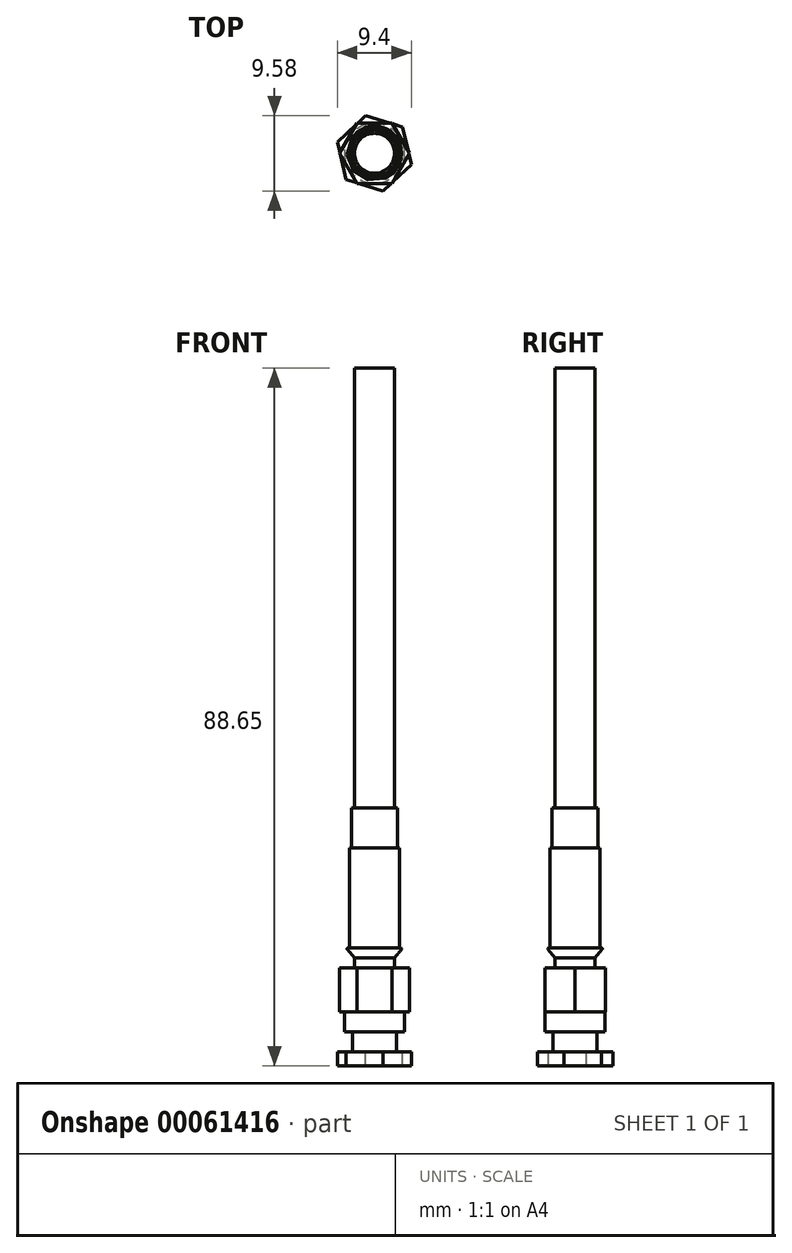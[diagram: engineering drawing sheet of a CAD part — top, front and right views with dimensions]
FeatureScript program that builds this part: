
annotation { "Feature Type Name" : "Feature", "Feature Type Description" : "" }
export const myFeature = defineFeature(function(context is Context, id is Id, definition is map)
    precondition{}
    {
        {
            var Q0;
            Q0=qCreatedBy(makeId("Top.planeOp"),FACE);
            var sketch = newSketch(context, id + "F0", { "sketchPlane" : qUnion([Q0])});
            skCircle(sketch, "E0", {"center": v(0, 0) * mm, "radius": 2.54 * mm});
            skSolve(sketch);
        }
        {
            var Q0;
            Q0 = qSketchRegion(id + "F0", true);
            extrude(context, id + "F1", {"entities" : qUnion([Q0]), "depth" : 76.2 * mm});
        }
        {
            var Q0;
            Q0=qCreatedBy(makeId("Top.planeOp"),FACE);
            var sketch = newSketch(context, id + "F2", { "sketchPlane" : qUnion([Q0])});
            skCircle(sketch, "E1.cCircle", {"center": v(0, 0) * mm, "radius": 3.85 * mm, "construction": true});
            skLineSegment(sketch, "E1.0", {"start": v(4.45, 0) * mm, "end": v(2.22, -3.85) * mm});
            skLineSegment(sketch, "E1.1", {"start": v(2.22, -3.85) * mm, "end": v(-2.22, -3.85) * mm});
            skLineSegment(sketch, "E1.2", {"start": v(-2.22, -3.85) * mm, "end": v(-4.45, 0) * mm});
            skLineSegment(sketch, "E1.3", {"start": v(-4.44, 0) * mm, "end": v(-2.22, 3.85) * mm});
            skLineSegment(sketch, "E1.4", {"start": v(-2.22, 3.85) * mm, "end": v(2.22, 3.85) * mm});
            skLineSegment(sketch, "E1.5", {"start": v(2.22, 3.85) * mm, "end": v(4.44, 0) * mm});
            skPoint(sketch, "E1.0.midPoint", {"position": v(3.33, -1.92) * mm});
            skSolve(sketch);
        }
        {
            var Q0;
            Q0 = qSketchRegion(id + "F2", true);
            extrude(context, id + "F3", {"entities" : qUnion([Q0]), "operationType" : NewBodyOperationType.ADD, "oppositeDirection" : true, "depth" : 5.6 * mm});
        }
        {
            var Q0;
            Q0=makeQuery(id+"F3.opExtrude","CAP_FACE",FACE,{"disambiguationData":[OSD([sQuery(id+"F2.wireOp",EDGE,"E1.0"),sQuery(id+"F2.wireOp",EDGE,"E1.1"),sQuery(id+"F2.wireOp",EDGE,"E1.2"),sQuery(id+"F2.wireOp",EDGE,"E1.3"),sQuery(id+"F2.wireOp",EDGE,"E1.4"),sQuery(id+"F2.wireOp",EDGE,"E1.5")])],"isStart":false});
            var sketch = newSketch(context, id + "F4", { "sketchPlane" : qUnion([Q0])});
            skCircle(sketch, "E2", {"center": v(0, 0) * mm, "radius": 3.81 * mm});
            skSolve(sketch);
        }
        {
            var Q0;
            Q0=makeQuery(id+"F4.imprint","IMPRINT",FACE,{"disambiguationData":[TD([[makeQuery(id+"F4.imprint","IMPRINT",EDGE,{"derivedFrom":sQuery(id+"F4.wireOp",EDGE,"E2")}),1.0]])]});
            extrude(context, id + "F5", {"entities" : qUnion([Q0]), "operationType" : NewBodyOperationType.ADD, "depth" : 2.54 * mm});
        }
        {
            var Q0;
            Q0=makeQuery(id+"F5.opExtrude","CAP_FACE",FACE,{"disambiguationData":[OSD([sQuery(id+"F4.wireOp",EDGE,"E2")])],"isStart":false});
            var sketch = newSketch(context, id + "F6", { "sketchPlane" : qUnion([Q0])});
            skCircle(sketch, "E3", {"center": v(0, 0) * mm, "radius": 2.8 * mm});
            skSolve(sketch);
        }
        {
            var Q0;
            Q0 = qSketchRegion(id + "F6", true);
            extrude(context, id + "F7", {"entities" : qUnion([Q0]), "operationType" : NewBodyOperationType.ADD, "depth" : 2.54 * mm});
        }
        {
            var Q0;
            Q0=makeQuery(id+"F7.opExtrude","CAP_FACE",FACE,{"disambiguationData":[OSD([sQuery(id+"F6.wireOp",EDGE,"E3")])],"isStart":false});
            var sketch = newSketch(context, id + "F8", { "sketchPlane" : qUnion([Q0])});
            skCircle(sketch, "E4.cCircle", {"center": v(0, 0) * mm, "radius": 4.26 * mm, "construction": true});
            skLineSegment(sketch, "E4.0", {"start": v(-4.7, -1.44) * mm, "end": v(-3.6, 3.35) * mm});
            skLineSegment(sketch, "E4.1", {"start": v(-3.6, 3.35) * mm, "end": v(1.1, 4.79) * mm});
            skLineSegment(sketch, "E4.2", {"start": v(1.1, 4.79) * mm, "end": v(4.7, 1.44) * mm});
            skLineSegment(sketch, "E4.3", {"start": v(4.7, 1.44) * mm, "end": v(3.6, -3.35) * mm});
            skLineSegment(sketch, "E4.4", {"start": v(3.6, -3.35) * mm, "end": v(-1.1, -4.79) * mm});
            skLineSegment(sketch, "E4.5", {"start": v(-1.1, -4.79) * mm, "end": v(-4.7, -1.44) * mm});
            skPoint(sketch, "E4.0.midPoint", {"position": v(-4.15, 0.96) * mm});
            skSolve(sketch);
        }
        {
            var Q0;
            Q0 = qSketchRegion(id + "F8", true);
            extrude(context, id + "F9", {"entities" : qUnion([Q0]), "operationType" : NewBodyOperationType.ADD, "depth" : 1.78 * mm});
        }
        {
            var Q0;
            Q0=makeQuery(id+"F3.opExtrude","CAP_FACE",FACE,{"disambiguationData":[OSD([sQuery(id+"F2.wireOp",EDGE,"E1.0"),sQuery(id+"F2.wireOp",EDGE,"E1.1"),sQuery(id+"F2.wireOp",EDGE,"E1.2"),sQuery(id+"F2.wireOp",EDGE,"E1.3"),sQuery(id+"F2.wireOp",EDGE,"E1.4"),sQuery(id+"F2.wireOp",EDGE,"E1.5")])],"isStart":true});
            cPlane(context, id + "F10", {"entities" : qUnion([Q0]), "cplaneType" : CPlaneType.OFFSET, "offset" : 1.27 * mm, "width" : 152.4 * mm, "height" : 152.4 * mm});
        }
        {
            var Q0;
            Q0=qCreatedBy(id+"F10.planeOp",FACE);
            var sketch = newSketch(context, id + "F11", { "sketchPlane" : qUnion([Q0])});
            skCircle(sketch, "E5", {"center": v(0, 0) * mm, "radius": 2.54 * mm});
            skSolve(sketch);
        }
        {
            var Q0;
            Q0 = qSketchRegion(id + "F11", true);
            extrude(context, id + "F12", {"entities" : qUnion([Q0]), "operationType" : NewBodyOperationType.ADD, "depth" : 1.27 * mm, "hasDraft" : true, "draftAngle" : 40 * degree});
        }
        {
            var Q0;
            Q0=makeQuery(id+"F12.opExtrude","CAP_EDGE",EDGE,{"disambiguationData":[OSD([sQuery(id+"F11.wireOp",EDGE,"E5")])],"isStart":false});
            fillet(context, id + "F13", {"entities" : qUnion([Q0]), "radius" : 0.13 * mm, "tangentPropagation" : true, "allowEdgeOverflow" : false});
        }
        {
            var Q0;
            Q0=makeQuery(id+"F12.opExtrude","CAP_FACE",FACE,{"disambiguationData":[OSD([sQuery(id+"F11.wireOp",EDGE,"E5")])],"isStart":false});
            var sketch = newSketch(context, id + "F14", { "sketchPlane" : qUnion([Q0])});
            skCircle(sketch, "E6", {"center": v(0, 0) * mm, "radius": 3.17 * mm});
            skSolve(sketch);
        }
        {
            var Q0;
            Q0 = qSketchRegion(id + "F14", true);
            extrude(context, id + "F15", {"entities" : qUnion([Q0]), "operationType" : NewBodyOperationType.ADD, "depth" : 12.7 * mm});
        }
        {
            var Q0;
            Q0=makeQuery(id+"F15.opExtrude","CAP_FACE",FACE,{"disambiguationData":[OSD([sQuery(id+"F14.wireOp",EDGE,"E6")])],"isStart":false});
            var sketch = newSketch(context, id + "F16", { "sketchPlane" : qUnion([Q0])});
            skCircle(sketch, "E7", {"center": v(0, 0) * mm, "radius": 2.92 * mm});
            skSolve(sketch);
        }
        {
            var Q0;
            Q0 = qSketchRegion(id + "F16", true);
            extrude(context, id + "F17", {"entities" : qUnion([Q0]), "operationType" : NewBodyOperationType.ADD, "depth" : 5.08 * mm});
        }
    });
